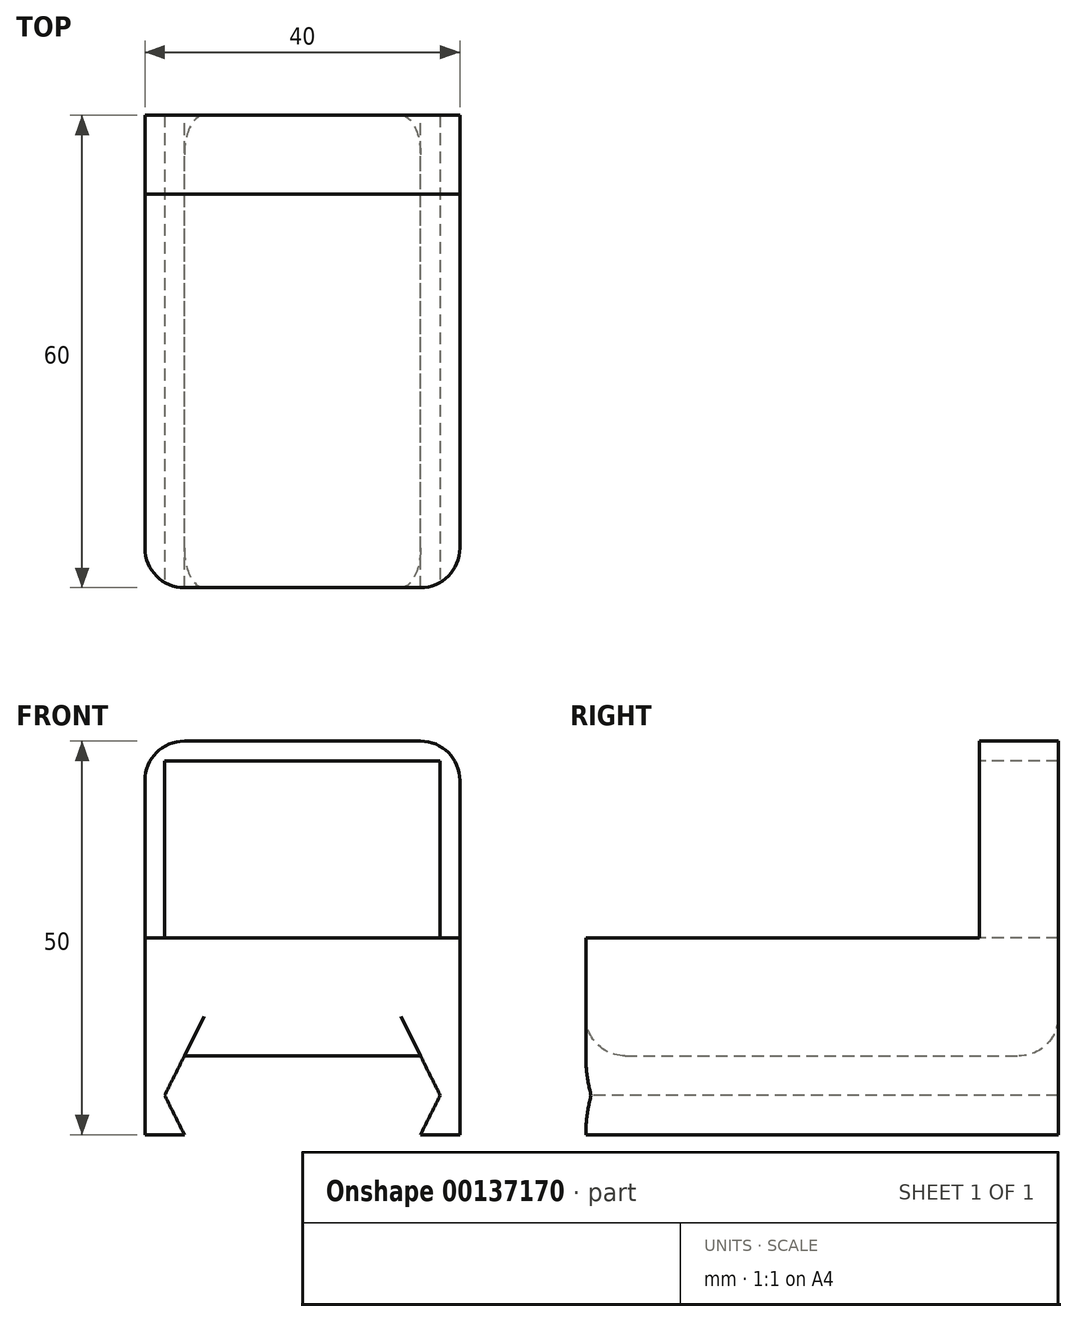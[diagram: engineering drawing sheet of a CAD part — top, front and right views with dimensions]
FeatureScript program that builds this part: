
annotation { "Feature Type Name" : "Feature", "Feature Type Description" : "" }
export const myFeature = defineFeature(function(context is Context, id is Id, definition is map)
    precondition{}
    {
        {
            var Q0;
            Q0=qCreatedBy(makeId("Front.planeOp"),FACE);
            var sketch = newSketch(context, id + "F0", { "sketchPlane" : qUnion([Q0])});
            skLineSegment(sketch, "E0.bottom", {"start": v(-20, 7.5) * mm, "end": v(20, 7.5) * mm});
            skLineSegment(sketch, "E0.top", {"start": v(-20, -7.5) * mm, "end": v(20, -7.5) * mm});
            skLineSegment(sketch, "E0.left", {"start": v(-20, 7.5) * mm, "end": v(-20, -7.5) * mm});
            skLineSegment(sketch, "E0.right", {"start": v(20, 7.5) * mm, "end": v(20, -7.5) * mm});
            skPoint(sketch, "E0.middle", {"position": v(0, 0) * mm});
            skSolve(sketch);
        }
        {
            var Q0;
            Q0 = qSketchRegion(id + "F0", true);
            extrude(context, id + "F1", {"entities" : qUnion([Q0]), "endBound" : BoundingType.SYMMETRIC, "depth" : 60 * mm});
        }
        {
            var Q0;
            Q0=makeQuery(id+"F1.opExtrude","SWEPT_FACE",FACE,{"disambiguationData":[OSD([sQuery(id+"F0.wireOp",EDGE,"E0.bottom")])]});
            var sketch = newSketch(context, id + "F2", { "sketchPlane" : qUnion([Q0])});
            skLineSegment(sketch, "E1.bottom", {"start": v(-20, 30) * mm, "end": v(-17.5, 30) * mm});
            skLineSegment(sketch, "E1.top", {"start": v(-20, 20) * mm, "end": v(-17.5, 20) * mm});
            skLineSegment(sketch, "E1.left", {"start": v(-20, 30) * mm, "end": v(-20, 20) * mm});
            skLineSegment(sketch, "E1.right", {"start": v(-17.5, 30) * mm, "end": v(-17.5, 20) * mm});
            skLineSegment(sketch, "E2.MirrorCS", {"start": v(17.5, 30) * mm, "end": v(17.5, 20) * mm});
            skLineSegment(sketch, "E3.MirrorCS", {"start": v(20, 30) * mm, "end": v(20, 20) * mm});
            skLineSegment(sketch, "E4.MirrorCS", {"start": v(20, 30) * mm, "end": v(17.5, 30) * mm});
            skLineSegment(sketch, "E5.MirrorCS", {"start": v(20, 20) * mm, "end": v(17.5, 20) * mm});
            skSolve(sketch);
        }
        {
            var Q0;
            Q0 = qSketchRegion(id + "F2", true);
            extrude(context, id + "F3", {"entities" : qUnion([Q0]), "operationType" : NewBodyOperationType.ADD, "depth" : 25 * mm});
        }
        {
            var Q0;
            Q0=makeQuery(id+"F3.opExtrude","SWEPT_FACE",FACE,{"disambiguationData":[OSD([sQuery(id+"F2.wireOp",EDGE,"E2.MirrorCS")])]});
            var sketch = newSketch(context, id + "F4", { "sketchPlane" : qUnion([Q0])});
            skLineSegment(sketch, "E6.bottom", {"start": v(-30, 32.5) * mm, "end": v(-20, 32.5) * mm});
            skLineSegment(sketch, "E6.top", {"start": v(-30, 30) * mm, "end": v(-20, 30) * mm});
            skLineSegment(sketch, "E6.left", {"start": v(-30, 32.5) * mm, "end": v(-30, 30) * mm});
            skLineSegment(sketch, "E6.right", {"start": v(-20, 32.5) * mm, "end": v(-20, 30) * mm});
            skSolve(sketch);
        }
        {
            var Q0;
            Q0 = qSketchRegion(id + "F4", true);
            extrude(context, id + "F5", {"entities" : qUnion([Q0]), "operationType" : NewBodyOperationType.ADD, "endBound" : BoundingType.UP_TO_NEXT, "depth" : 25 * mm});
        }
        {
            var Q0;
            Q0=makeQuery(id+"F1.opExtrude","SWEPT_FACE",FACE,{"disambiguationData":[OSD([sQuery(id+"F0.wireOp",EDGE,"E0.top")])]});
            var sketch = newSketch(context, id + "F6", { "sketchPlane" : qUnion([Q0])});
            skLineSegment(sketch, "E7.bottom", {"start": v(-20, 30) * mm, "end": v(-15, 30) * mm});
            skLineSegment(sketch, "E7.top", {"start": v(-20, -30) * mm, "end": v(-15, -30) * mm});
            skLineSegment(sketch, "E7.left", {"start": v(-20, 30) * mm, "end": v(-20, -30) * mm});
            skLineSegment(sketch, "E7.right", {"start": v(-15, 30) * mm, "end": v(-15, -30) * mm});
            skLineSegment(sketch, "E8.MirrorCS", {"start": v(20, 30) * mm, "end": v(15, 30) * mm});
            skLineSegment(sketch, "E9.MirrorCS", {"start": v(20, 30) * mm, "end": v(20, -30) * mm});
            skLineSegment(sketch, "E10.MirrorCS", {"start": v(15, 30) * mm, "end": v(15, -30) * mm});
            skLineSegment(sketch, "E11.MirrorCS", {"start": v(20, -30) * mm, "end": v(15, -30) * mm});
            skSolve(sketch);
        }
        {
            var Q0;
            Q0=makeQuery(id+"F6.imprint","IMPRINT",FACE,{"disambiguationData":[TD([[makeQuery(id+"F6.imprint","IMPRINT",EDGE,{"derivedFrom":sQuery(id+"F6.wireOp",EDGE,"E7.bottom")}),-1.0]])]});
            var Q1;
            Q1=makeQuery(id+"F6.imprint","IMPRINT",FACE,{"disambiguationData":[TD([[makeQuery(id+"F6.imprint","IMPRINT",EDGE,{"derivedFrom":sQuery(id+"F6.wireOp",EDGE,"E8.MirrorCS")}),-1.0]])]});
            extrude(context, id + "F7", {"entities" : qUnion([Q0, Q1]), "operationType" : NewBodyOperationType.ADD, "depth" : 10 * mm});
        }
        {
            var Q0;
            Q0=makeQuery(id+"F7.boolean.opBoolean","MERGE",FACE,{"derivedFrom":[makeQuery(id+"F1.opExtrude","CAP_FACE",FACE,{"disambiguationData":[OSD([sQuery(id+"F0.wireOp",EDGE,"E0.bottom"),sQuery(id+"F0.wireOp",EDGE,"E0.top"),sQuery(id+"F0.wireOp",EDGE,"E0.left"),sQuery(id+"F0.wireOp",EDGE,"E0.right")])],"isStart":false}),makeQuery(id+"F7.opExtrude","SWEPT_FACE",FACE,{"disambiguationData":[OSD([sQuery(id+"F6.wireOp",EDGE,"E7.bottom")])]}),makeQuery(id+"F7.opExtrude","SWEPT_FACE",FACE,{"disambiguationData":[OSD([sQuery(id+"F6.wireOp",EDGE,"E8.MirrorCS")])]})]});
            var sketch = newSketch(context, id + "F8", { "sketchPlane" : qUnion([Q0])});
            skLineSegment(sketch, "E12", {"start": v(-15, -7.5) * mm, "end": v(-20, -7.5) * mm, "construction": true});
            skLineSegment(sketch, "E13", {"start": v(15, -7.5) * mm, "end": v(20, -7.5) * mm, "construction": true});
            skLineSegment(sketch, "E14", {"start": v(-20, -7.5) * mm, "end": v(-15, -17.5) * mm});
            skLineSegment(sketch, "E15", {"start": v(-15, -7.5) * mm, "end": v(-20, -17.5) * mm});
            skLineSegment(sketch, "E16", {"start": v(15, -7.5) * mm, "end": v(20, -17.5) * mm});
            skLineSegment(sketch, "E17", {"start": v(20, -7.5) * mm, "end": v(15, -17.5) * mm});
            skSolve(sketch);
        }
        {
            var Q0;
            {var subQ1=sQuery(id+"F6.wireOp",EDGE,"E7.bottom");var subQ2=sQuery(id+"F0.wireOp",EDGE,"E0.top");var subQ3=makeQuery(id+"F7.opExtrude","SWEPT_EDGE",EDGE,{"disambiguationData":[OSD([subQ2,subQ1,sQuery(id+"F6.wireOp",EDGE,"E7.right")])]});Q0=makeQuery(id+"F8.imprint","IMPRINT",FACE,{"disambiguationData":[TD([[makeQuery(id+"F8.imprint","IMPRINT",EDGE,{"derivedFrom":subQ3}),1.0]])]});}
            var Q1;
            {var subQ1=sQuery(id+"F0.wireOp",EDGE,"E0.top");var subQ2=sQuery(id+"F6.wireOp",EDGE,"E8.MirrorCS");var subQ3=makeQuery(id+"F7.opExtrude","SWEPT_EDGE",EDGE,{"disambiguationData":[OSD([subQ1,subQ2,sQuery(id+"F6.wireOp",EDGE,"E10.MirrorCS")])]});Q1=makeQuery(id+"F8.imprint","IMPRINT",FACE,{"disambiguationData":[TD([[makeQuery(id+"F8.imprint","IMPRINT",EDGE,{"derivedFrom":subQ3}),-1.0]])]});}
            extrude(context, id + "F9", {"entities" : qUnion([Q0, Q1]), "operationType" : NewBodyOperationType.REMOVE, "endBound" : BoundingType.THROUGH_ALL, "oppositeDirection" : true, "depth" : 25 * mm});
        }
        {
            var Q0;
            Q0=makeQuery(id+"F3.opExtrude","CAP_EDGE",EDGE,{"disambiguationData":[OSD([sQuery(id+"F2.wireOp",EDGE,"E3.MirrorCS")])],"isStart":false});
            var Q1;
            Q1=makeQuery(id+"F3.opExtrude","CAP_EDGE",EDGE,{"disambiguationData":[OSD([sQuery(id+"F2.wireOp",EDGE,"E1.left")])],"isStart":false});
            var Q2;
            Q2=makeQuery(id+"F5.opExtrude","TWEAK_EDGE",EDGE,{"derivedFrom":[makeQuery(id+"F3.opExtrude","SWEPT_FACE",FACE,{"disambiguationData":[OSD([sQuery(id+"F2.wireOp",EDGE,"E1.right")])]}),makeQuery(id+"F4.imprint","IMPRINT",EDGE,{"derivedFrom":sQuery(id+"F4.wireOp",EDGE,"E6.top")})]});
            var Q3;
            Q3=makeQuery(id+"F5.opExtrude","CAP_EDGE",EDGE,{"disambiguationData":[OSD([sQuery(id+"F4.wireOp",EDGE,"E6.top")])],"isStart":true});
            var Q4;
            Q4=makeQuery(id+"F3.opExtrude","CAP_EDGE",EDGE,{"disambiguationData":[OSD([sQuery(id+"F2.wireOp",EDGE,"E2.MirrorCS")])],"isStart":true});
            var Q5;
            Q5=makeQuery(id+"F3.opExtrude","CAP_EDGE",EDGE,{"disambiguationData":[OSD([sQuery(id+"F2.wireOp",EDGE,"E1.right")])],"isStart":true});
            var Q6;
            Q6=makeQuery(id+"F7.boolean.opBoolean","MERGE",EDGE,{"derivedFrom":[makeQuery(id+"F1.opExtrude","CAP_EDGE",EDGE,{"disambiguationData":[OSD([sQuery(id+"F0.wireOp",EDGE,"E0.right")])],"isStart":false}),makeQuery(id+"F7.opExtrude","SWEPT_EDGE",EDGE,{"disambiguationData":[OSD([sQuery(id+"F6.wireOp",EDGE,"E8.MirrorCS"),sQuery(id+"F6.wireOp",EDGE,"E9.MirrorCS")])]})]});
            var Q7;
            Q7=makeQuery(id+"F7.boolean.opBoolean","MERGE",EDGE,{"derivedFrom":[makeQuery(id+"F1.opExtrude","CAP_EDGE",EDGE,{"disambiguationData":[OSD([sQuery(id+"F0.wireOp",EDGE,"E0.left")])],"isStart":false}),makeQuery(id+"F7.opExtrude","SWEPT_EDGE",EDGE,{"disambiguationData":[OSD([sQuery(id+"F6.wireOp",EDGE,"E7.bottom"),sQuery(id+"F6.wireOp",EDGE,"E7.left")])]})]});
            var Q8;
            Q8=makeQuery(id+"F1.opExtrude","CAP_EDGE",EDGE,{"disambiguationData":[OSD([sQuery(id+"F0.wireOp",EDGE,"E0.top")])],"isStart":false});
            var Q9;
            Q9=makeQuery(id+"F1.opExtrude","CAP_EDGE",EDGE,{"disambiguationData":[OSD([sQuery(id+"F0.wireOp",EDGE,"E0.top")])],"isStart":true});
            fillet(context, id + "F10", {"entities" : qUnion([Q0, Q1, Q2, Q3, Q4, Q5, Q6, Q7, Q8, Q9]), "radius" : 5 * mm, "tangentPropagation" : true, "allowEdgeOverflow" : false});
        }
    });
